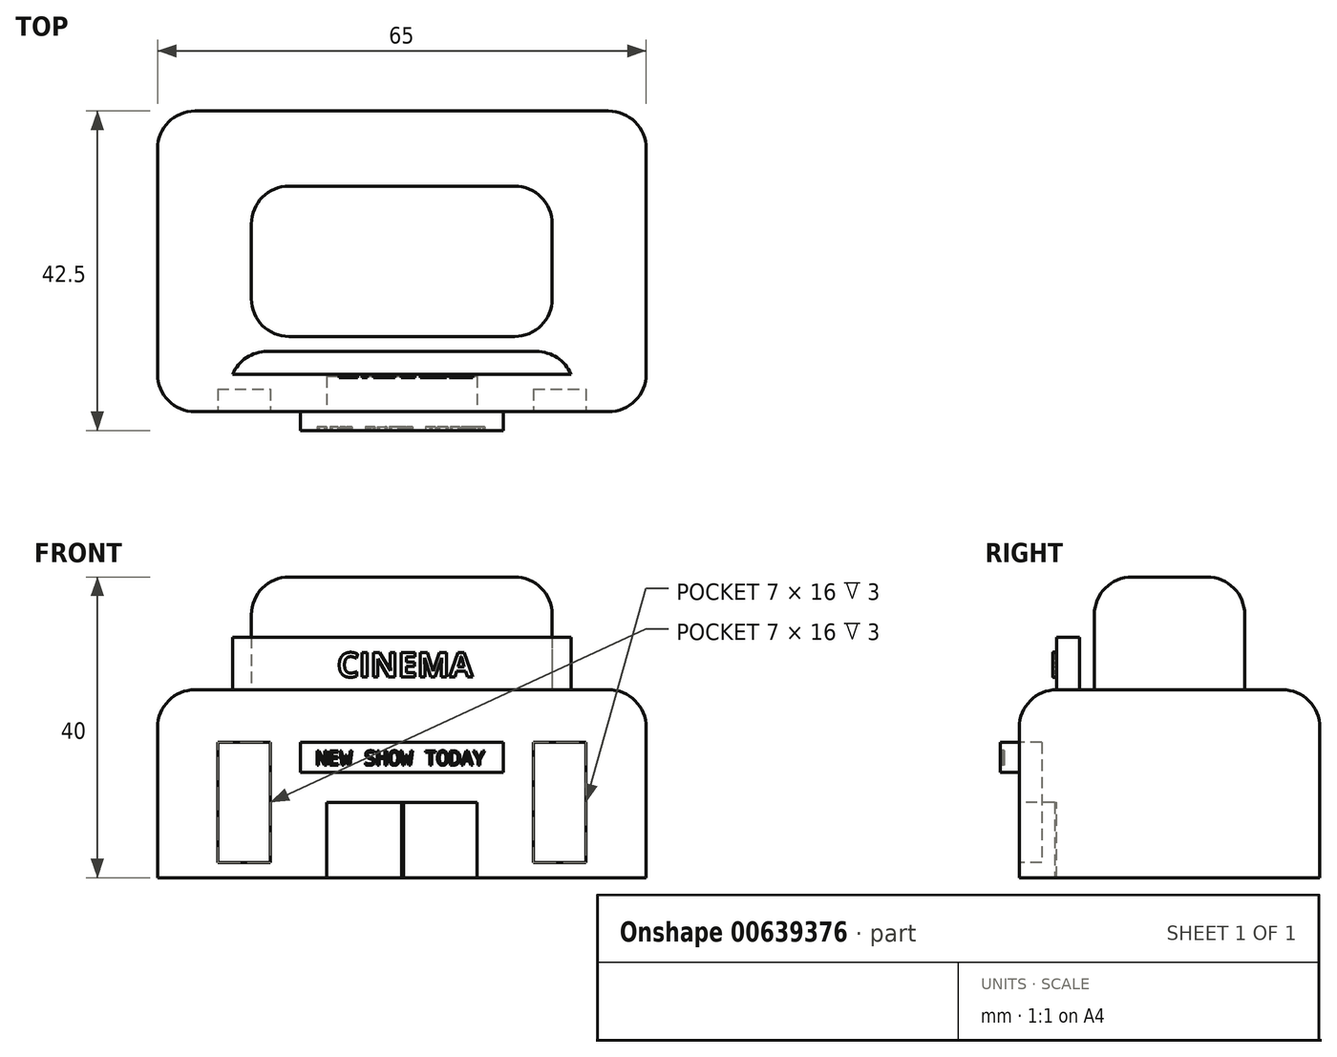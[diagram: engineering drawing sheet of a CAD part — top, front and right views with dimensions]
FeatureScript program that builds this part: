
annotation { "Feature Type Name" : "Feature", "Feature Type Description" : "" }
export const myFeature = defineFeature(function(context is Context, id is Id, definition is map)
    precondition{}
    {
        {
            var Q0;
            Q0=qCreatedBy(makeId("Top.planeOp"),FACE);
            var sketch = newSketch(context, id + "F0", { "sketchPlane" : qUnion([Q0])});
            skLineSegment(sketch, "E0.bottom", {"start": v(-25.15, 20.97) * mm, "end": v(39.85, 20.97) * mm});
            skLineSegment(sketch, "E0.top", {"start": v(-25.15, -19.03) * mm, "end": v(39.85, -19.03) * mm});
            skLineSegment(sketch, "E0.left", {"start": v(-25.15, 20.97) * mm, "end": v(-25.15, -19.03) * mm});
            skLineSegment(sketch, "E0.right", {"start": v(39.85, 20.97) * mm, "end": v(39.85, -19.03) * mm});
            skSolve(sketch);
        }
        {
            var Q0;
            Q0 = qSketchRegion(id + "F0", true);
            extrude(context, id + "F1", {"entities" : qUnion([Q0]), "depth" : 25 * mm, "offsetDistance" : 25 * mm});
        }
        {
            var Q0;
            Q0=makeQuery(id+"F1.opExtrude","SWEPT_EDGE",EDGE,{"disambiguationData":[OSD([sQuery(id+"F0.wireOp",EDGE,"E0.top"),sQuery(id+"F0.wireOp",EDGE,"E0.left")])]});
            var Q1;
            Q1=makeQuery(id+"F1.opExtrude","SWEPT_EDGE",EDGE,{"disambiguationData":[OSD([sQuery(id+"F0.wireOp",EDGE,"E0.top"),sQuery(id+"F0.wireOp",EDGE,"E0.right")])]});
            var Q2;
            Q2=makeQuery(id+"F1.opExtrude","CAP_EDGE",EDGE,{"disambiguationData":[OSD([sQuery(id+"F0.wireOp",EDGE,"E0.top")])],"isStart":false});
            var Q3;
            Q3=makeQuery(id+"F1.opExtrude","CAP_EDGE",EDGE,{"disambiguationData":[OSD([sQuery(id+"F0.wireOp",EDGE,"E0.right")])],"isStart":false});
            var Q4;
            Q4=makeQuery(id+"F1.opExtrude","CAP_EDGE",EDGE,{"disambiguationData":[OSD([sQuery(id+"F0.wireOp",EDGE,"E0.bottom")])],"isStart":false});
            var Q5;
            Q5=makeQuery(id+"F1.opExtrude","CAP_EDGE",EDGE,{"disambiguationData":[OSD([sQuery(id+"F0.wireOp",EDGE,"E0.left")])],"isStart":false});
            var Q6;
            Q6=makeQuery(id+"F1.opExtrude","SWEPT_EDGE",EDGE,{"disambiguationData":[OSD([sQuery(id+"F0.wireOp",EDGE,"E0.bottom"),sQuery(id+"F0.wireOp",EDGE,"E0.left")])]});
            var Q7;
            Q7=makeQuery(id+"F1.opExtrude","SWEPT_EDGE",EDGE,{"disambiguationData":[OSD([sQuery(id+"F0.wireOp",EDGE,"E0.bottom"),sQuery(id+"F0.wireOp",EDGE,"E0.right")])]});
            fillet(context, id + "F2", {"entities" : qUnion([Q0, Q1, Q2, Q3, Q4, Q5, Q6, Q7]), "radius" : 5 * mm, "tangentPropagation" : true, "allowEdgeOverflow" : false});
        }
        {
            var Q0;
            Q0=makeQuery(id+"F1.opExtrude","SWEPT_FACE",FACE,{"disambiguationData":[OSD([sQuery(id+"F0.wireOp",EDGE,"E0.top")])]});
            var sketch = newSketch(context, id + "F3", { "sketchPlane" : qUnion([Q0])});
            skLineSegment(sketch, "E1", {"start": v(-20.15, 10) * mm, "end": v(34.85, 10) * mm});
            skPoint(sketch, "E1.endSnap0", {"position": v(34.85, 10) * mm});
            skLineSegment(sketch, "E2", {"start": v(7.35, 10) * mm, "end": v(7.35, 0) * mm});
            skPoint(sketch, "E3.orphan", {"position": v(7.35, 20) * mm});
            skPoint(sketch, "E4.orphan", {"position": v(60, 10) * mm});
            skLineSegment(sketch, "E5.bottom", {"start": v(7.35, 10) * mm, "end": v(17.35, 10) * mm});
            skLineSegment(sketch, "E5.top", {"start": v(7.35, 0) * mm, "end": v(17.35, 0) * mm});
            skLineSegment(sketch, "E5.right", {"start": v(17.35, 10) * mm, "end": v(17.35, 0) * mm});
            skLineSegment(sketch, "E6.bottom", {"start": v(7.35, 10) * mm, "end": v(-2.65, 10) * mm});
            skLineSegment(sketch, "E6.top", {"start": v(7.35, 0) * mm, "end": v(-2.65, 0) * mm});
            skLineSegment(sketch, "E6.right", {"start": v(-2.65, 10) * mm, "end": v(-2.65, 0) * mm});
            skSolve(sketch);
        }
        {
            var Q0;
            Q0 = qSketchRegion(id + "F3", true);
            extrude(context, id + "F4", {"entities" : qUnion([Q0]), "operationType" : NewBodyOperationType.REMOVE, "oppositeDirection" : true, "depth" : 5 * mm, "offsetDistance" : 25 * mm});
        }
        {
            var Q0;
            Q0=makeQuery(id+"F1.opExtrude","SWEPT_FACE",FACE,{"disambiguationData":[OSD([sQuery(id+"F0.wireOp",EDGE,"E0.top")])]});
            var sketch = newSketch(context, id + "F5", { "sketchPlane" : qUnion([Q0])});
            skLineSegment(sketch, "E7", {"start": v(34.85, 20) * mm, "end": v(31.85, 20) * mm});
            skLineSegment(sketch, "E8", {"start": v(31.85, 18) * mm, "end": v(31.85, 2) * mm});
            skLineSegment(sketch, "E9", {"start": v(31.85, 20) * mm, "end": v(24.85, 20) * mm});
            skLineSegment(sketch, "E10", {"start": v(24.85, 18) * mm, "end": v(24.85, 2) * mm});
            skLineSegment(sketch, "E11", {"start": v(24.85, 2) * mm, "end": v(31.85, 2) * mm});
            skLineSegment(sketch, "E12", {"start": v(24.85, 18) * mm, "end": v(31.85, 18) * mm});
            skPoint(sketch, "E13.orphan", {"position": v(24.85, 0) * mm});
            skPoint(sketch, "E14.orphan", {"position": v(31.85, 0) * mm});
            skLineSegment(sketch, "E15", {"start": v(-17.15, 18) * mm, "end": v(-17.15, 2) * mm});
            skLineSegment(sketch, "E16", {"start": v(-17.15, 18) * mm, "end": v(-10.15, 18) * mm});
            skLineSegment(sketch, "E17", {"start": v(-10.15, 18) * mm, "end": v(-10.15, 2) * mm});
            skLineSegment(sketch, "E18", {"start": v(-17.15, 2) * mm, "end": v(-10.15, 2) * mm});
            skPoint(sketch, "E19.orphan", {"position": v(-17.15, 20) * mm});
            skPoint(sketch, "E20.orphan", {"position": v(-10.15, 0) * mm});
            skPoint(sketch, "E21.orphan", {"position": v(-17.15, 0) * mm});
            skPoint(sketch, "E22.orphan", {"position": v(-17.15, 19.07) * mm});
            skSolve(sketch);
        }
        {
            var Q0;
            Q0 = qSketchRegion(id + "F5", true);
            extrude(context, id + "F6", {"entities" : qUnion([Q0]), "operationType" : NewBodyOperationType.REMOVE, "oppositeDirection" : true, "depth" : 2.5 * mm, "offsetDistance" : 25 * mm});
        }
        {
            var Q0;
            Q0 = qSketchRegion(id + "F5", true);
            extrude(context, id + "F7", {"entities" : qUnion([Q0]), "operationType" : NewBodyOperationType.REMOVE, "oppositeDirection" : true, "depth" : 3 * mm, "offsetDistance" : 25 * mm});
        }
        {
            var Q0;
            Q0=makeQuery(id+"F1.opExtrude","CAP_FACE",FACE,{"disambiguationData":[OSD([sQuery(id+"F0.wireOp",EDGE,"E0.bottom"),sQuery(id+"F0.wireOp",EDGE,"E0.top"),sQuery(id+"F0.wireOp",EDGE,"E0.left"),sQuery(id+"F0.wireOp",EDGE,"E0.right")])],"isStart":false});
            var sketch = newSketch(context, id + "F8", { "sketchPlane" : qUnion([Q0])});
            skLineSegment(sketch, "E23", {"start": v(7.35, 0.97) * mm, "end": v(-12.65, 0.97) * mm});
            skPoint(sketch, "E23.endSnap0", {"position": v(-20.15, 0.97) * mm});
            skLineSegment(sketch, "E24", {"start": v(7.35, 0.97) * mm, "end": v(27.35, 0.97) * mm});
            skPoint(sketch, "E25.orphan", {"position": v(34.85, 15.97) * mm});
            skPoint(sketch, "E26.start.orphan", {"position": v(-20.15, -14.03) * mm});
            skLineSegment(sketch, "E27.bottom", {"start": v(-12.65, 0.97) * mm, "end": v(27.35, 0.97) * mm});
            skLineSegment(sketch, "E27.top", {"start": v(-12.65, 10.97) * mm, "end": v(27.35, 10.97) * mm});
            skLineSegment(sketch, "E27.left", {"start": v(-12.65, 0.97) * mm, "end": v(-12.65, 10.97) * mm});
            skLineSegment(sketch, "E27.right", {"start": v(27.35, 0.97) * mm, "end": v(27.35, 10.97) * mm});
            skLineSegment(sketch, "E28.top", {"start": v(-12.65, -9.03) * mm, "end": v(27.35, -9.03) * mm});
            skLineSegment(sketch, "E28.left", {"start": v(-12.65, 0.97) * mm, "end": v(-12.65, -9.03) * mm});
            skLineSegment(sketch, "E28.right", {"start": v(27.35, 0.97) * mm, "end": v(27.35, -9.03) * mm});
            skSolve(sketch);
        }
        {
            var Q0;
            Q0 = qSketchRegion(id + "F8", true);
            extrude(context, id + "F9", {"entities" : qUnion([Q0]), "operationType" : NewBodyOperationType.ADD, "depth" : 15 * mm, "offsetDistance" : 25 * mm});
        }
        {
            var Q0;
            Q0=makeQuery(id+"F9.opExtrude","CAP_EDGE",EDGE,{"disambiguationData":[OSD([sQuery(id+"F8.wireOp",EDGE,"E28.top")])],"isStart":false});
            var Q1;
            Q1=makeQuery(id+"F9.opExtrude","SWEPT_EDGE",EDGE,{"disambiguationData":[OSD([sQuery(id+"F8.wireOp",EDGE,"E28.top"),sQuery(id+"F8.wireOp",EDGE,"E28.right")])]});
            var Q2;
            Q2=makeQuery(id+"F9.opExtrude","SWEPT_EDGE",EDGE,{"disambiguationData":[OSD([sQuery(id+"F8.wireOp",EDGE,"E28.top"),sQuery(id+"F8.wireOp",EDGE,"E28.left")])]});
            var Q3;
            Q3=makeQuery(id+"F9.opExtrude","CAP_EDGE",EDGE,{"disambiguationData":[OSD([sQuery(id+"F8.wireOp",EDGE,"E27.right"),sQuery(id+"F8.wireOp",EDGE,"E28.right")])],"isStart":false});
            var Q4;
            Q4=makeQuery(id+"F9.opExtrude","SWEPT_EDGE",EDGE,{"disambiguationData":[OSD([sQuery(id+"F8.wireOp",EDGE,"E27.top"),sQuery(id+"F8.wireOp",EDGE,"E27.right")])]});
            var Q5;
            Q5=makeQuery(id+"F9.opExtrude","SWEPT_EDGE",EDGE,{"disambiguationData":[OSD([sQuery(id+"F8.wireOp",EDGE,"E27.top"),sQuery(id+"F8.wireOp",EDGE,"E27.left")])]});
            var Q6;
            Q6=makeQuery(id+"F9.opExtrude","CAP_EDGE",EDGE,{"disambiguationData":[OSD([sQuery(id+"F8.wireOp",EDGE,"E27.top")])],"isStart":false});
            var Q7;
            Q7=makeQuery(id+"F9.opExtrude","CAP_EDGE",EDGE,{"disambiguationData":[OSD([sQuery(id+"F8.wireOp",EDGE,"E27.left"),sQuery(id+"F8.wireOp",EDGE,"E28.left")])],"isStart":false});
            fillet(context, id + "F10", {"entities" : qUnion([Q0, Q1, Q2, Q3, Q4, Q5, Q6, Q7]), "radius" : 5 * mm, "tangentPropagation" : true, "allowEdgeOverflow" : false});
        }
        {
            var Q0;
            Q0=makeQuery(id+"F1.opExtrude","CAP_FACE",FACE,{"disambiguationData":[OSD([sQuery(id+"F0.wireOp",EDGE,"E0.bottom"),sQuery(id+"F0.wireOp",EDGE,"E0.top"),sQuery(id+"F0.wireOp",EDGE,"E0.left"),sQuery(id+"F0.wireOp",EDGE,"E0.right")])],"isStart":false});
            var sketch = newSketch(context, id + "F11", { "sketchPlane" : qUnion([Q0])});
            skLineSegment(sketch, "E29", {"start": v(-20.15, -14.03) * mm, "end": v(-15.15, -14.03) * mm});
            skLineSegment(sketch, "E30", {"start": v(-15.15, -14.03) * mm, "end": v(-15.15, -11.03) * mm});
            skLineSegment(sketch, "E31", {"start": v(34.85, -14.03) * mm, "end": v(29.85, -14.03) * mm});
            skLineSegment(sketch, "E32", {"start": v(29.85, -14.03) * mm, "end": v(29.85, -11.03) * mm});
            skLineSegment(sketch, "E33", {"start": v(29.85, -11.03) * mm, "end": v(-15.15, -11.03) * mm});
            skLineSegment(sketch, "E34", {"start": v(-15.15, -14.03) * mm, "end": v(29.85, -14.03) * mm});
            skSolve(sketch);
        }
        {
            var Q0;
            Q0 = qSketchRegion(id + "F11", true);
            extrude(context, id + "F12", {"entities" : qUnion([Q0]), "operationType" : NewBodyOperationType.ADD, "depth" : 7 * mm, "offsetDistance" : 25 * mm});
        }
        {
            var Q0;
            Q0=makeQuery(id+"F12.opExtrude","SWEPT_EDGE",EDGE,{"disambiguationData":[OSD([sQuery(id+"F11.wireOp",EDGE,"E32"),sQuery(id+"F11.wireOp",EDGE,"E33")])]});
            var Q1;
            Q1=makeQuery(id+"F12.opExtrude","SWEPT_EDGE",EDGE,{"disambiguationData":[OSD([sQuery(id+"F11.wireOp",EDGE,"E30"),sQuery(id+"F11.wireOp",EDGE,"E33")])]});
            fillet(context, id + "F13", {"entities" : qUnion([Q0, Q1]), "radius" : 5 * mm, "tangentPropagation" : true, "allowEdgeOverflow" : false});
        }
        {
            var Q0;
            Q0=makeQuery(id+"F12.opExtrude","SWEPT_FACE",FACE,{"disambiguationData":[OSD([sQuery(id+"F11.wireOp",EDGE,"E34")])]});
            var sketch = newSketch(context, id + "F14", { "sketchPlane" : qUnion([Q0])});
            skText(sketch, "E35", { "text": "CINEMA", "fontName": "OpenSans-Bold.ttf"});
            const initialGuessF14  = {"E35": [-0.00124, 0.0267, 1, 0, 0.00327]};
            skSetInitialGuess(sketch, initialGuessF14);
            skSolve(sketch);
        }
        {
            var Q0;
            Q0 = qSketchRegion(id + "F14", true);
            extrude(context, id + "F15", {"entities" : qUnion([Q0]), "operationType" : NewBodyOperationType.ADD, "depth" : 0.5 * mm, "offsetDistance" : 25 * mm});
        }
        {
            var Q0;
            Q0=makeQuery(id+"F1.opExtrude","SWEPT_FACE",FACE,{"disambiguationData":[OSD([sQuery(id+"F0.wireOp",EDGE,"E0.top")])]});
            var sketch = newSketch(context, id + "F16", { "sketchPlane" : qUnion([Q0])});
            skLineSegment(sketch, "E36", {"start": v(-6.15, 18) * mm, "end": v(20.85, 18) * mm});
            skLineSegment(sketch, "E37", {"start": v(24.85, 18) * mm, "end": v(24.85, 14) * mm});
            skLineSegment(sketch, "E38", {"start": v(20.85, 14) * mm, "end": v(-6.15, 14) * mm});
            skLineSegment(sketch, "E39", {"start": v(-6.15, 15.93) * mm, "end": v(-6.15, 18) * mm});
            skLineSegment(sketch, "E40", {"start": v(-6.15, 18) * mm, "end": v(-6.15, 14) * mm});
            skLineSegment(sketch, "E41", {"start": v(20.85, 16) * mm, "end": v(20.85, 18) * mm});
            skLineSegment(sketch, "E42", {"start": v(20.85, 18) * mm, "end": v(20.85, 14) * mm});
            skPoint(sketch, "E43.start.orphan", {"position": v(24.85, 16) * mm});
            skPoint(sketch, "E44.orphan", {"position": v(-10.15, 14) * mm});
            skSolve(sketch);
        }
        {
            var Q0;
            Q0 = qSketchRegion(id + "F16", true);
            extrude(context, id + "F17", {"entities" : qUnion([Q0]), "operationType" : NewBodyOperationType.ADD, "depth" : 2.5 * mm, "offsetDistance" : 25 * mm});
        }
        {
            var Q0;
            Q0=makeQuery(id+"F17.opExtrude","CAP_FACE",FACE,{"disambiguationData":[OSD([sQuery(id+"F16.wireOp",EDGE,"E36"),sQuery(id+"F16.wireOp",EDGE,"E38"),sQuery(id+"F16.wireOp",EDGE,"E40"),sQuery(id+"F16.wireOp",EDGE,"E42")])],"isStart":false});
            var sketch = newSketch(context, id + "F18", { "sketchPlane" : qUnion([Q0])});
            skText(sketch, "E45", { "text": "NEW SHOW TODAY", "fontName": "DroidSansMono.ttf"});
            const initialGuessF18  = {"E45": [-0.0041, 0.01497, 1, 0, 0.00193]};
            skSetInitialGuess(sketch, initialGuessF18);
            skSolve(sketch);
        }
        {
            var Q0;
            Q0 = qSketchRegion(id + "F18", true);
            extrude(context, id + "F19", {"entities" : qUnion([Q0]), "operationType" : NewBodyOperationType.REMOVE, "oppositeDirection" : true, "depth" : 0.5 * mm, "offsetDistance" : 25 * mm});
        }
        {
            var Q0;
            Q0=makeQuery(id+"F4.boolean.opBoolean","COPY",FACE,{"derivedFrom":makeQuery(id+"F4.opExtrude","CAP_FACE",FACE,{"disambiguationData":[OSD([sQuery(id+"F3.wireOp",EDGE,"E5.bottom"),sQuery(id+"F3.wireOp",EDGE,"E5.top"),sQuery(id+"F3.wireOp",EDGE,"E5.right"),sQuery(id+"F3.wireOp",EDGE,"E6.bottom"),sQuery(id+"F3.wireOp",EDGE,"E6.top"),sQuery(id+"F3.wireOp",EDGE,"E6.right")])],"isStart":false})});
            var sketch = newSketch(context, id + "F20", { "sketchPlane" : qUnion([Q0])});
            skLineSegment(sketch, "E46", {"start": v(-2.65, 10) * mm, "end": v(7.35, 10) * mm});
            skLineSegment(sketch, "E47", {"start": v(7.35, 10) * mm, "end": v(7.35, 0) * mm});
            skLineSegment(sketch, "E48", {"start": v(7.35, 0) * mm, "end": v(7.55, 0) * mm});
            skLineSegment(sketch, "E49", {"start": v(7.55, 0) * mm, "end": v(7.55, 10) * mm});
            skSolve(sketch);
        }
        {
            var Q0;
            Q0 = qSketchRegion(id + "F20", true);
            var Q1;
            Q1=makeQuery(id+"F20.imprint","IMPRINT",FACE,{"disambiguationData":[TD([[makeQuery(id+"F20.imprint","IMPRINT",EDGE,{"derivedFrom":sQuery(id+"F20.wireOp",EDGE,"E46")}),-1.0]])]});
            var Q2;
            {var subQ0=sQuery(id+"F20.wireOp",EDGE,"E49");Q2=makeQuery(id+"F20.imprint","IMPRINT",FACE,{"disambiguationData":[TD([[makeQuery(id+"F20.imprint","IMPRINT",EDGE,{"derivedFrom":subQ0}),-1.0]])]});}
            extrude(context, id + "F21", {"entities" : qUnion([Q0, Q1, Q2]), "operationType" : NewBodyOperationType.ADD, "depth" : 0.3 * mm, "offsetDistance" : 25 * mm});
        }
    });
